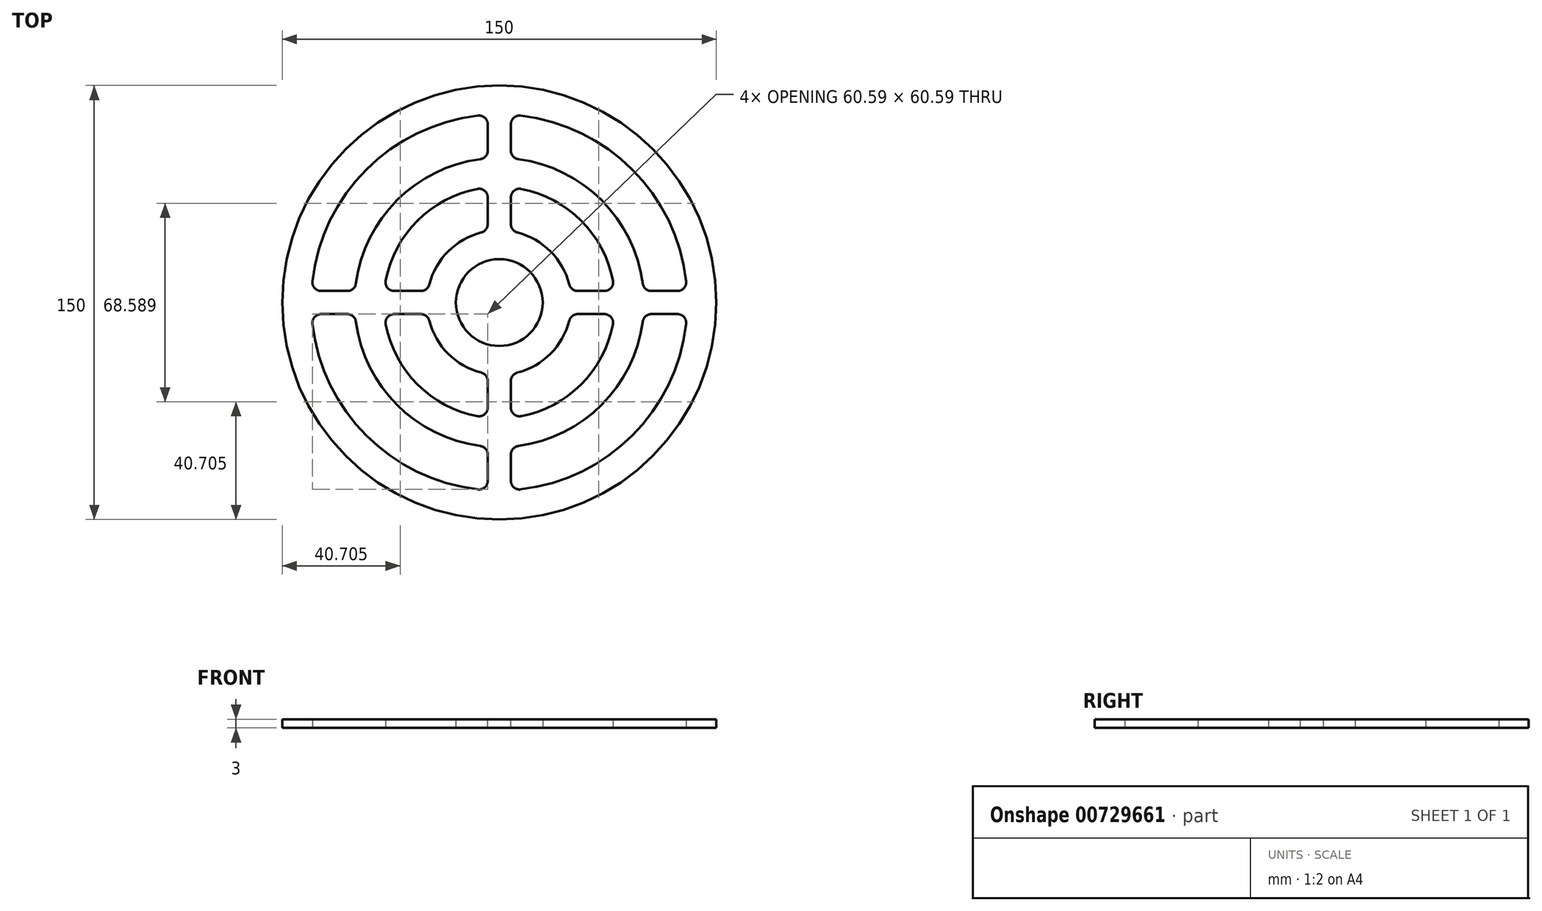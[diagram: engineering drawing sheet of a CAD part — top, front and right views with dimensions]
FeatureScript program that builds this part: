
annotation { "Feature Type Name" : "Feature", "Feature Type Description" : "" }
export const myFeature = defineFeature(function(context is Context, id is Id, definition is map)
    precondition{}
    {
        {
            var Q0;
            Q0=qCreatedBy(makeId("Top.planeOp"),FACE);
            var sketch = newSketch(context, id + "F0", { "sketchPlane" : qUnion([Q0])});
            skCircle(sketch, "E0", {"center": v(0, 0) * mm, "radius": 40 * mm});
            skCircle(sketch, "E1", {"center": v(0, 0) * mm, "radius": 50 * mm});
            skCircle(sketch, "E2", {"center": v(0, 0) * mm, "radius": 65 * mm});
            skCircle(sketch, "E3", {"center": v(0, 0) * mm, "radius": 75 * mm});
            skCircle(sketch, "E4", {"center": v(0, 0) * mm, "radius": 25 * mm});
            skCircle(sketch, "E5", {"center": v(0, 0) * mm, "radius": 15 * mm});
            skLineSegment(sketch, "E6", {"start": v(-4, 64.88) * mm, "end": v(-4, 49.84) * mm});
            skLineSegment(sketch, "E7", {"start": v(4, 64.88) * mm, "end": v(4, 49.84) * mm});
            skLineSegment(sketch, "E8", {"start": v(-4, 39.8) * mm, "end": v(-4, 24.68) * mm});
            skLineSegment(sketch, "E9", {"start": v(4, 39.8) * mm, "end": v(4, 24.68) * mm});
            skLineSegment(sketch, "E10", {"start": v(4, -24.68) * mm, "end": v(4, -39.8) * mm});
            skLineSegment(sketch, "E11", {"start": v(-4, -24.68) * mm, "end": v(-4, -39.8) * mm});
            skLineSegment(sketch, "E12", {"start": v(4, -49.84) * mm, "end": v(4, -64.88) * mm});
            skLineSegment(sketch, "E13", {"start": v(-4, -49.84) * mm, "end": v(-4, -64.88) * mm});
            skLineSegment(sketch, "E14", {"start": v(64.88, 4) * mm, "end": v(49.84, 4) * mm});
            skLineSegment(sketch, "E15", {"start": v(64.88, -4) * mm, "end": v(49.84, -4) * mm});
            skLineSegment(sketch, "E16", {"start": v(39.8, 4) * mm, "end": v(24.68, 4) * mm});
            skLineSegment(sketch, "E17", {"start": v(39.8, -4) * mm, "end": v(24.68, -4) * mm});
            skLineSegment(sketch, "E18", {"start": v(-24.68, 4) * mm, "end": v(-39.8, 4) * mm});
            skLineSegment(sketch, "E19", {"start": v(-24.68, -4) * mm, "end": v(-39.8, -4) * mm});
            skLineSegment(sketch, "E20", {"start": v(-49.84, 4) * mm, "end": v(-64.88, 4) * mm});
            skLineSegment(sketch, "E21", {"start": v(-49.84, -4) * mm, "end": v(-64.88, -4) * mm});
            skSolve(sketch);
        }
        {
            var Q0;
            Q0=makeQuery(id+"F0.imprint","IMPRINT",FACE,{"disambiguationData":[TD([[makeQuery(id+"F0.imprint","IMPRINT",EDGE,{"derivedFrom":sQuery(id+"F0.wireOp",EDGE,"E3")}),1.0]])]});
            var Q1;
            {var subQ0=sQuery(id+"F0.wireOp",EDGE,"E6");Q1=makeQuery(id+"F0.imprint","IMPRINT",FACE,{"disambiguationData":[TD([[makeQuery(id+"F0.imprint","IMPRINT",EDGE,{"derivedFrom":subQ0}),1.0]])]});}
            var Q2;
            {var subQ0=sQuery(id+"F0.wireOp",EDGE,"E0");var subQ1=makeQuery(id+"F0.imprint","INTERSECT",VERTEX,{"derivedFrom":[subQ0,sQuery(id+"F0.wireOp",EDGE,"E8")]});Q2=makeQuery(id+"F0.imprint","IMPRINT",FACE,{"disambiguationData":[TD([[makeQuery(id+"F0.imprint","IMPRINT",EDGE,{"disambiguationData":[TD([[subQ1,1.0]])],"derivedFrom":subQ0}),-1.0]])]});}
            var Q3;
            {var subQ0=sQuery(id+"F0.wireOp",EDGE,"E8");Q3=makeQuery(id+"F0.imprint","IMPRINT",FACE,{"disambiguationData":[TD([[makeQuery(id+"F0.imprint","IMPRINT",EDGE,{"derivedFrom":subQ0}),1.0]])]});}
            var Q4;
            Q4=makeQuery(id+"F0.imprint","IMPRINT",FACE,{"disambiguationData":[TD([[makeQuery(id+"F0.imprint","IMPRINT",EDGE,{"derivedFrom":sQuery(id+"F0.wireOp",EDGE,"E5")}),-1.0]])]});
            var Q5;
            {var subQ0=sQuery(id+"F0.wireOp",EDGE,"E18");Q5=makeQuery(id+"F0.imprint","IMPRINT",FACE,{"disambiguationData":[TD([[makeQuery(id+"F0.imprint","IMPRINT",EDGE,{"derivedFrom":subQ0}),1.0]])]});}
            var Q6;
            {var subQ0=sQuery(id+"F0.wireOp",EDGE,"E20");Q6=makeQuery(id+"F0.imprint","IMPRINT",FACE,{"disambiguationData":[TD([[makeQuery(id+"F0.imprint","IMPRINT",EDGE,{"derivedFrom":subQ0}),1.0]])]});}
            var Q7;
            {var subQ0=sQuery(id+"F0.wireOp",EDGE,"E10");Q7=makeQuery(id+"F0.imprint","IMPRINT",FACE,{"disambiguationData":[TD([[makeQuery(id+"F0.imprint","IMPRINT",EDGE,{"derivedFrom":subQ0}),-1.0]])]});}
            var Q8;
            {var subQ0=sQuery(id+"F0.wireOp",EDGE,"E12");Q8=makeQuery(id+"F0.imprint","IMPRINT",FACE,{"disambiguationData":[TD([[makeQuery(id+"F0.imprint","IMPRINT",EDGE,{"derivedFrom":subQ0}),-1.0]])]});}
            var Q9;
            {var subQ0=sQuery(id+"F0.wireOp",EDGE,"E16");Q9=makeQuery(id+"F0.imprint","IMPRINT",FACE,{"disambiguationData":[TD([[makeQuery(id+"F0.imprint","IMPRINT",EDGE,{"derivedFrom":subQ0}),1.0]])]});}
            var Q10;
            {var subQ0=sQuery(id+"F0.wireOp",EDGE,"E14");Q10=makeQuery(id+"F0.imprint","IMPRINT",FACE,{"disambiguationData":[TD([[makeQuery(id+"F0.imprint","IMPRINT",EDGE,{"derivedFrom":subQ0}),1.0]])]});}
            extrude(context, id + "F1", {"entities" : qUnion([Q0, Q1, Q2, Q3, Q4, Q5, Q6, Q7, Q8, Q9, Q10]), "depth" : 3 * mm, "offsetDistance" : 25 * mm});
        }
        {
            var Q0;
            Q0=makeQuery(id+"F1.opExtrude","SWEPT_EDGE",EDGE,{"disambiguationData":[OSD([sQuery(id+"F0.wireOp",EDGE,"E2"),sQuery(id+"F0.wireOp",EDGE,"E20")])]});
            var Q1;
            Q1=makeQuery(id+"F1.opExtrude","SWEPT_EDGE",EDGE,{"disambiguationData":[OSD([sQuery(id+"F0.wireOp",EDGE,"E0"),sQuery(id+"F0.wireOp",EDGE,"E18")])]});
            var Q2;
            Q2=makeQuery(id+"F1.opExtrude","SWEPT_EDGE",EDGE,{"disambiguationData":[OSD([sQuery(id+"F0.wireOp",EDGE,"E4"),sQuery(id+"F0.wireOp",EDGE,"E9")])]});
            var Q3;
            Q3=makeQuery(id+"F1.opExtrude","SWEPT_EDGE",EDGE,{"disambiguationData":[OSD([sQuery(id+"F0.wireOp",EDGE,"E1"),sQuery(id+"F0.wireOp",EDGE,"E14")])]});
            var Q4;
            Q4=makeQuery(id+"F1.opExtrude","SWEPT_EDGE",EDGE,{"disambiguationData":[OSD([sQuery(id+"F0.wireOp",EDGE,"E4"),sQuery(id+"F0.wireOp",EDGE,"E16")])]});
            var Q5;
            Q5=makeQuery(id+"F1.opExtrude","SWEPT_EDGE",EDGE,{"disambiguationData":[OSD([sQuery(id+"F0.wireOp",EDGE,"E0"),sQuery(id+"F0.wireOp",EDGE,"E10")])]});
            var Q6;
            Q6=makeQuery(id+"F1.opExtrude","SWEPT_EDGE",EDGE,{"disambiguationData":[OSD([sQuery(id+"F0.wireOp",EDGE,"E2"),sQuery(id+"F0.wireOp",EDGE,"E12")])]});
            var Q7;
            Q7=makeQuery(id+"F1.opExtrude","SWEPT_EDGE",EDGE,{"disambiguationData":[OSD([sQuery(id+"F0.wireOp",EDGE,"E1"),sQuery(id+"F0.wireOp",EDGE,"E7")])]});
            var Q8;
            Q8=makeQuery(id+"F1.opExtrude","SWEPT_EDGE",EDGE,{"disambiguationData":[OSD([sQuery(id+"F0.wireOp",EDGE,"E2"),sQuery(id+"F0.wireOp",EDGE,"E15")])]});
            var Q9;
            Q9=makeQuery(id+"F1.opExtrude","SWEPT_EDGE",EDGE,{"disambiguationData":[OSD([sQuery(id+"F0.wireOp",EDGE,"E0"),sQuery(id+"F0.wireOp",EDGE,"E17")])]});
            var Q10;
            Q10=makeQuery(id+"F1.opExtrude","SWEPT_EDGE",EDGE,{"disambiguationData":[OSD([sQuery(id+"F0.wireOp",EDGE,"E0"),sQuery(id+"F0.wireOp",EDGE,"E8")])]});
            var Q11;
            Q11=makeQuery(id+"F1.opExtrude","SWEPT_EDGE",EDGE,{"disambiguationData":[OSD([sQuery(id+"F0.wireOp",EDGE,"E4"),sQuery(id+"F0.wireOp",EDGE,"E11")])]});
            var Q12;
            Q12=makeQuery(id+"F1.opExtrude","SWEPT_EDGE",EDGE,{"disambiguationData":[OSD([sQuery(id+"F0.wireOp",EDGE,"E1"),sQuery(id+"F0.wireOp",EDGE,"E13")])]});
            var Q13;
            Q13=makeQuery(id+"F1.opExtrude","SWEPT_EDGE",EDGE,{"disambiguationData":[OSD([sQuery(id+"F0.wireOp",EDGE,"E1"),sQuery(id+"F0.wireOp",EDGE,"E21")])]});
            var Q14;
            Q14=makeQuery(id+"F1.opExtrude","SWEPT_EDGE",EDGE,{"disambiguationData":[OSD([sQuery(id+"F0.wireOp",EDGE,"E2"),sQuery(id+"F0.wireOp",EDGE,"E6")])]});
            var Q15;
            Q15=makeQuery(id+"F1.opExtrude","SWEPT_EDGE",EDGE,{"disambiguationData":[OSD([sQuery(id+"F0.wireOp",EDGE,"E2"),sQuery(id+"F0.wireOp",EDGE,"E7")])]});
            var Q16;
            Q16=makeQuery(id+"F1.opExtrude","SWEPT_EDGE",EDGE,{"disambiguationData":[OSD([sQuery(id+"F0.wireOp",EDGE,"E2"),sQuery(id+"F0.wireOp",EDGE,"E21")])]});
            var Q17;
            Q17=makeQuery(id+"F1.opExtrude","SWEPT_EDGE",EDGE,{"disambiguationData":[OSD([sQuery(id+"F0.wireOp",EDGE,"E0"),sQuery(id+"F0.wireOp",EDGE,"E19")])]});
            var Q18;
            Q18=makeQuery(id+"F1.opExtrude","SWEPT_EDGE",EDGE,{"disambiguationData":[OSD([sQuery(id+"F0.wireOp",EDGE,"E4"),sQuery(id+"F0.wireOp",EDGE,"E17")])]});
            var Q19;
            Q19=makeQuery(id+"F1.opExtrude","SWEPT_EDGE",EDGE,{"disambiguationData":[OSD([sQuery(id+"F0.wireOp",EDGE,"E1"),sQuery(id+"F0.wireOp",EDGE,"E15")])]});
            var Q20;
            Q20=makeQuery(id+"F1.opExtrude","SWEPT_EDGE",EDGE,{"disambiguationData":[OSD([sQuery(id+"F0.wireOp",EDGE,"E1"),sQuery(id+"F0.wireOp",EDGE,"E12")])]});
            var Q21;
            Q21=makeQuery(id+"F1.opExtrude","SWEPT_EDGE",EDGE,{"disambiguationData":[OSD([sQuery(id+"F0.wireOp",EDGE,"E2"),sQuery(id+"F0.wireOp",EDGE,"E13")])]});
            var Q22;
            Q22=makeQuery(id+"F1.opExtrude","SWEPT_EDGE",EDGE,{"disambiguationData":[OSD([sQuery(id+"F0.wireOp",EDGE,"E0"),sQuery(id+"F0.wireOp",EDGE,"E11")])]});
            var Q23;
            Q23=makeQuery(id+"F1.opExtrude","SWEPT_EDGE",EDGE,{"disambiguationData":[OSD([sQuery(id+"F0.wireOp",EDGE,"E4"),sQuery(id+"F0.wireOp",EDGE,"E18")])]});
            var Q24;
            Q24=makeQuery(id+"F1.opExtrude","SWEPT_EDGE",EDGE,{"disambiguationData":[OSD([sQuery(id+"F0.wireOp",EDGE,"E0"),sQuery(id+"F0.wireOp",EDGE,"E16")])]});
            var Q25;
            Q25=makeQuery(id+"F1.opExtrude","SWEPT_EDGE",EDGE,{"disambiguationData":[OSD([sQuery(id+"F0.wireOp",EDGE,"E2"),sQuery(id+"F0.wireOp",EDGE,"E14")])]});
            var Q26;
            Q26=makeQuery(id+"F1.opExtrude","SWEPT_EDGE",EDGE,{"disambiguationData":[OSD([sQuery(id+"F0.wireOp",EDGE,"E4"),sQuery(id+"F0.wireOp",EDGE,"E8")])]});
            var Q27;
            Q27=makeQuery(id+"F1.opExtrude","SWEPT_EDGE",EDGE,{"disambiguationData":[OSD([sQuery(id+"F0.wireOp",EDGE,"E1"),sQuery(id+"F0.wireOp",EDGE,"E6")])]});
            var Q28;
            Q28=makeQuery(id+"F1.opExtrude","SWEPT_EDGE",EDGE,{"disambiguationData":[OSD([sQuery(id+"F0.wireOp",EDGE,"E1"),sQuery(id+"F0.wireOp",EDGE,"E20")])]});
            var Q29;
            Q29=makeQuery(id+"F1.opExtrude","SWEPT_EDGE",EDGE,{"disambiguationData":[OSD([sQuery(id+"F0.wireOp",EDGE,"E4"),sQuery(id+"F0.wireOp",EDGE,"E10")])]});
            var Q30;
            Q30=makeQuery(id+"F1.opExtrude","SWEPT_EDGE",EDGE,{"disambiguationData":[OSD([sQuery(id+"F0.wireOp",EDGE,"E0"),sQuery(id+"F0.wireOp",EDGE,"E9")])]});
            var Q31;
            Q31=makeQuery(id+"F1.opExtrude","SWEPT_EDGE",EDGE,{"disambiguationData":[OSD([sQuery(id+"F0.wireOp",EDGE,"E4"),sQuery(id+"F0.wireOp",EDGE,"E19")])]});
            fillet(context, id + "F2", {"entities" : qUnion([Q0, Q1, Q2, Q3, Q4, Q5, Q6, Q7, Q8, Q9, Q10, Q11, Q12, Q13, Q14, Q15, Q16, Q17, Q18, Q19, Q20, Q21, Q22, Q23, Q24, Q25, Q26, Q27, Q28, Q29, Q30, Q31]), "radius" : 3 * mm, "tangentPropagation" : true, "allowEdgeOverflow" : false});
        }
    });
